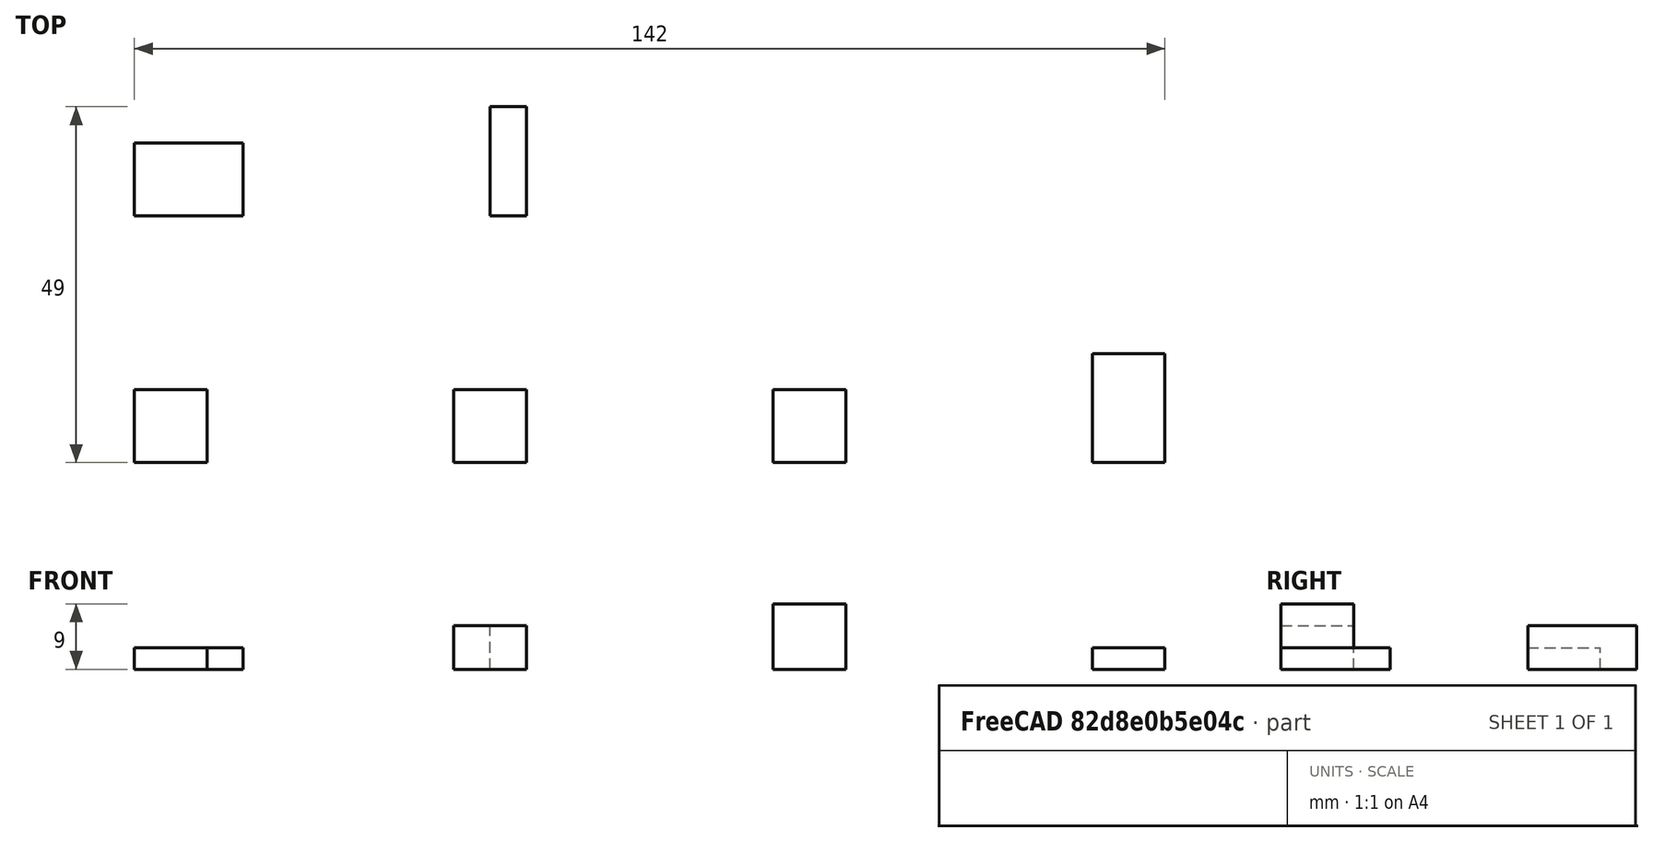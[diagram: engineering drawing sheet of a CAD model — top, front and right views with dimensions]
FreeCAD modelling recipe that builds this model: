
FCSTD DOCUMENT  (FreeCAD 0.16R6703 (Git))
Label: quads-test-result
License: All rights reserved
LicenseURL: http://en.wikipedia.org/wiki/All_rights_reserved
objects: Part::Box×6
note: 6 computed .brp shape members not serialized (recipe doc carries the construction recipe); baked Part::Feature solids carry a one-line shape summary decoded from their .brp

FEATURE [Part::Box] Box  label="Cube"
  Height = 3
  Length = 10
  Width = 10
FEATURE [Part::Box] Box001  label="Cube001"
  Height = 6
  Length = 10
  Placement = pos=(44,0,0) rot=(0,0,1;0rad)
  Width = 10
FEATURE [Part::Box] Box002  label="Cube002"
  Height = 9
  Length = 10
  Placement = pos=(88,0,0) rot=(0,0,1;0rad)
  Width = 10
FEATURE [Part::Box] Box003  label="Cube003"
  Height = 3
  Length = 10
  Placement = pos=(132,0,0) rot=(0,0,1;0rad)
  Width = 15
FEATURE [Part::Box] Box004  label="Cube004"
  Height = 3
  Length = 15
  Placement = pos=(0,34,0) rot=(0,0,1;0rad)
  Width = 10
FEATURE [Part::Box] Box005  label="Cube005"
  Height = 6
  Length = 5
  Placement = pos=(49,34,0) rot=(0,0,1;0rad)
  Width = 15
